# Revit family: RN 22132 KRV-Ventil
name_source: partatom
category: Rohrzubehör
units: mm (PartAtom-declared; Revit-internal decimal feet)

## family parameters
Arbeitsebenenbasiert = Nein
Beim Laden mit Abzugskörper schneiden = Nein
Bemaßung runder Anschluss = Durchmesser verwenden
Gemeinsam genutzt = Nein
Immer vertikal = Ja
Teiletyp = Ventil - Zerlegung in

## types (6) — shared parameters
1.010.00.2 Blattnummer der Richtlinie = 17
1.010.00.3 Ausgabedatum (Monat) der Richtlinie = 201601
1.010.00.4 Herstellername = R. Nussbaum AG
1.010.00.5 Revisionsdatum der Datei = 20190528
1.010.00.6 Webadresse des Herstellers = http://www.nussbaum.ch
1.100.00.3 Sortiernummer für Anzeigereihenfolge = 4
1.100.00.4 Produktbezeichnung = Sicherungs- und Ringleitungsarmaturen
1.960/3L.00.8 Link (URL) = https://www.nussbaum.ch
17.700.00.4 Armaturentyp = 6
17.700.00.7 Maximale Betriebstemperatur TB [°C] = 90
17.700.00.8 Maximaler Betriebsdruck (Arbeitsdruck) ps [1.0 · 105 Pa] = 16
Connector Visibility = Nein
EnclosingSpace Visibility = Nein
Hersteller = R. Nussbauzm AG
URL = https://www.nussbaum.ch

## per-type parameters (varying)
| type | 1.800.00.3 TGA-Nummer | 1.810.00.3 Hersteller-Bestellnummer | 1.810.00.4 DATANORM-Nummer | 1.810.00.5 StLB-Nummer | 1.810.00.6 GTIN-Nummer | 17.700.00.30 Produktbeschreibung | 17.700.00.5 Nennweite DN | 17.700.00.6 kvs-Wert [m3/h] | CONNECTOR0_DIAMETER_dX_0r | CONNECTOR0_dX_00 | CONNECTOR0_dX_01 | CONNECTOR0_ref_dX | CONNECTOR1_DIAMETER_dX_0r | CONNECTOR1_dX_00 | CONNECTOR1_dX_01 | CONNECTOR1_ref_dX | Modell | R. Nussbaum AG 22132.04 de Visibility | R. Nussbaum AG 22132.05 de Visibility | R. Nussbaum AG 22132.06 de Visibility | R. Nussbaum AG 22132.07 de Visibility | R. Nussbaum AG 22132.08 de Visibility | R. Nussbaum AG 22132.09 de Visibility | Typenkommentare |
| DN 15 | 0040230000000000000000000000020070000000000000000100000000 | 22132.04 | 22132.04 | 621.183 | 7612945737120 | 22132.04, KRV-Ventil, mit Entleerventil, DN=15, Rp=½ | 15 | 5.4 | 15 mm  [stored 0.0492126 ft] | 35 mm | 22 mm | 22 mm | 15 mm  [stored 0.0492126 ft] | 22 mm | 35 mm | 22 mm | 22132.04 | Ja | Nein | Nein | Nein | Nein | Nein | KRV-VentilDN 15 |
| DN 20 | 0040230000000000000000000000020070000000000000000200000000 | 22132.05 | 22132.05 | 621.184 | 7612945737335 | 22132.05, KRV-Ventil, mit Entleerventil, DN=20, Rp=¾ | 20 | 10.8 | 20 mm | 42 mm | 27 mm | 27 mm | 20 mm | 28 mm | 43 mm | 28 mm | 22132.05 | Nein | Ja | Nein | Nein | Nein | Nein | KRV-VentilDN 20 |
| DN 25 | 0040230000000000000000000000020070000000000000000300000000 | 22132.06 | 22132.06 | 621.185 | 7612945737649 | 22132.06, KRV-Ventil, mit Entleerventil, DN=25, Rp=1 | 25 | 16.8 | 25 mm  [stored 0.082021 ft] | 50 mm | 33 mm | 33 mm | 25 mm  [stored 0.082021 ft] | 33 mm | 50 mm | 33 mm | 22132.06 | Nein | Nein | Ja | Nein | Nein | Nein | KRV-VentilDN 25 |
| DN 32 | 0040230000000000000000000000020070000000000000000400000000 | 22132.07 | 22132.07 | 621.186 | 7612945735324 | 22132.07, KRV-Ventil, mit Entleerventil, DN=32, Rp=1¼ | 32 | 31.2 | 32 mm | 57 mm | 38 mm | 38 mm | 32 mm | 39 mm | 58 mm | 39 mm | 22132.07 | Nein | Nein | Nein | Ja | Nein | Nein | KRV-VentilDN 32 |
| DN 40 | 0040230000000000000000000000020070000000000000000500000000 | 22132.08 | 22132.08 | 621.187 | 7612945733702 | 22132.08, KRV-Ventil, mit Entleerventil, DN=40, Rp=1½ | 40 | 45 | 40 mm | 65 mm | 46 mm | 46 mm | 40 mm | 46 mm | 65 mm | 46 mm | 22132.08 | Nein | Nein | Nein | Nein | Ja | Nein | KRV-VentilDN 40 |
| DN 50 | 0040230000000000000000000000020070000000000000000600000000 | 22132.09 | 22132.09 | 621.188 | 7612945734082 | 22132.09, KRV-Ventil, mit Entleerventil, DN=50, Rp=2 | 50 | 69 | 50 mm | 75 mm | 51 mm | 51 mm | 50 mm | 51 mm | 75 mm | 51 mm | 22132.09 | Nein | Nein | Nein | Nein | Nein | Ja | KRV-VentilDN 50 |

note: [stored X ft] marks values corroborated as IEEE doubles in the binary element streams (Revit-internal decimal feet)

## geometry (parser evidence)
native form markers: Sweep x1
no freeform markers — native parametric forms only
